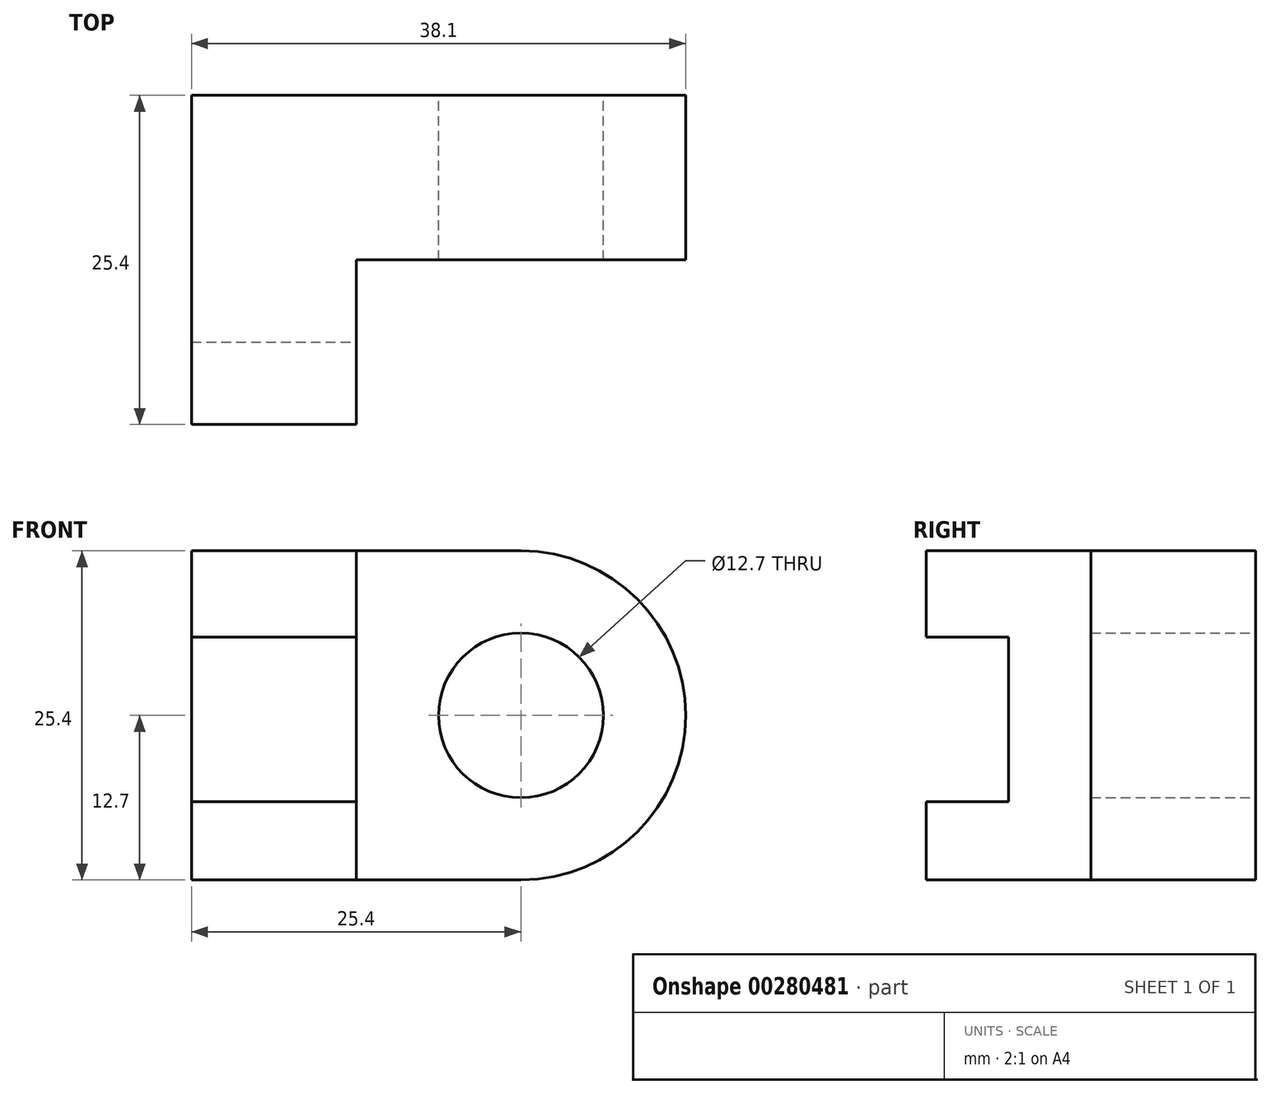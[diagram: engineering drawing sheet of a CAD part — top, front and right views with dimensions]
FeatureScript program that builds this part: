
annotation { "Feature Type Name" : "Feature", "Feature Type Description" : "" }
export const myFeature = defineFeature(function(context is Context, id is Id, definition is map)
    precondition{}
    {
        {
            var Q0;
            Q0=qCreatedBy(makeId("Front.planeOp"),FACE);
            var sketch = newSketch(context, id + "F0", { "sketchPlane" : qUnion([Q0])});
            skLineSegment(sketch, "E0", {"start": v(0, 0) * mm, "end": v(0, 25.4) * mm});
            skLineSegment(sketch, "E1", {"start": v(0, 25.4) * mm, "end": v(12.7, 25.4) * mm});
            skArc(sketch, "E2", {"start": v(12.7, 0) * mm, "mid": v(25.4, 12.7) * mm, "end": v(12.7, 25.4) * mm});
            skLineSegment(sketch, "E3", {"start": v(12.7, 0) * mm, "end": v(0, 0) * mm});
            skCircle(sketch, "E4", {"center": v(12.7, 12.7) * mm, "radius": 6.35 * mm});
            skSolve(sketch);
        }
        {
            var Q0;
            Q0=makeQuery(id+"F0.imprint","IMPRINT",FACE,{"disambiguationData":[TD([[makeQuery(id+"F0.imprint","IMPRINT",EDGE,{"derivedFrom":sQuery(id+"F0.wireOp",EDGE,"E0")}),-1.0]])]});
            extrude(context, id + "F1", {"entities" : qUnion([Q0]), "depth" : 12.7 * mm});
        }
        {
            var Q0;
            Q0=qCreatedBy(makeId("Front.planeOp"),FACE);
            var sketch = newSketch(context, id + "F2", { "sketchPlane" : qUnion([Q0])});
            skLineSegment(sketch, "E5", {"start": v(0, 0) * mm, "end": v(-12.7, 0) * mm});
            skLineSegment(sketch, "E6", {"start": v(-12.7, 0) * mm, "end": v(-12.7, 25.4) * mm});
            skLineSegment(sketch, "E7", {"start": v(-12.7, 25.4) * mm, "end": v(0, 25.4) * mm});
            skLineSegment(sketch, "E8", {"start": v(0, 25.4) * mm, "end": v(0, 0) * mm});
            skSolve(sketch);
        }
        {
            var Q0;
            Q0 = qSketchRegion(id + "F2", true);
            extrude(context, id + "F3", {"entities" : qUnion([Q0]), "operationType" : NewBodyOperationType.ADD, "depth" : 25.4 * mm});
        }
        {
            var Q0;
            Q0=qCreatedBy(makeId("Right.planeOp"),FACE);
            var sketch = newSketch(context, id + "F4", { "sketchPlane" : qUnion([Q0])});
            skLineSegment(sketch, "E9", {"start": v(-25.4, 18.75) * mm, "end": v(-25.4, 6.05) * mm});
            skLineSegment(sketch, "E10", {"start": v(-25.4, 18.75) * mm, "end": v(-19.05, 18.75) * mm});
            skLineSegment(sketch, "E11", {"start": v(-19.05, 18.75) * mm, "end": v(-19.05, 6.05) * mm});
            skLineSegment(sketch, "E12", {"start": v(-19.05, 6.05) * mm, "end": v(-25.4, 6.05) * mm});
            skSolve(sketch);
        }
        {
            var Q0;
            Q0 = qSketchRegion(id + "F4", true);
            extrude(context, id + "F5", {"entities" : qUnion([Q0]), "operationType" : NewBodyOperationType.REMOVE, "oppositeDirection" : true, "depth" : 25.4 * mm});
        }
    });
